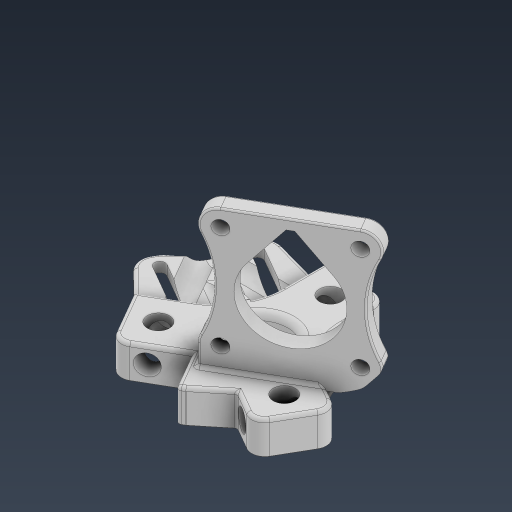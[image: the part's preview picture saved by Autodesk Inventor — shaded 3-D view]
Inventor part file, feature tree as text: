
AUTODESK INVENTOR PART (.ipt)
format: ipt  version: 2024 (Build 280153000, 153)  size: 945,152 bytes
history: native  units: mm
features: sketch x18, extrude x16, fillet x10, chamfer x6, hole x4, projected_geometry x4, plane x3, pattern_circular x2, mirror x1
ambient origin geometry x8: Origin, YZ Plane, XZ Plane, XY Plane, X Axis, Y Axis, Z Axis, Center Point
bodies: Solid1 (feature_tree)
feature tree (64):
  sketch  "Sketch1"  dims[d0=22.0mm d1=12.0mm]
  extrude  "Extrusion1"  Depth=12.0mm
  hole  "Hole1"  [1 undecoded]
  sketch  "Sketch2"  dims[d2=10.0mm d3=0.0mm]
  plane  "Work Plane1"
  plane  "Work Plane2"
  plane  "Work Plane3"
  sketch  "Sketch3"  dims[d4=6.65mm d5=6.0mm d6=4.0mm d7=2.0mm d8=90.0deg d9=8.0mm d10=20.594885mm d11=90.0deg]
  extrude  "Extrusion3"  TaperAngle=90.0deg  [1 undecoded]
  pattern_circular  "Circular Pattern2"  Count=3 Angle=360.0deg
  sketch  "Sketch31"  dims[d85=2.0mm d86=10.0mm d87=12.9mm d88=7.0mm d90=9.15mm d91=10.0mm d92=0.0mm d93=0.0mm d94=0.0mm d113=1.0mm d114=0.0mm d115=5.0mm d116=9.0mm d118=41.0mm d121=42.5mm d122=0.0mm d124=2.0mm d125=6.0mm d126=4.0mm d127=2.0mm d128=90.0deg d129=9.394mm d130=0.0mm d131=3.1mm d132=6.5mm d133=5.0mm d134=2.5mm d153=4.2mm d154=6.0mm d155=8.0mm d156=4.0mm d157=90.0deg d158=9.394mm d159=0.0mm d160=5.0mm d161=31.0mm d162=31.0mm d163=5.0mm d164=30.0mm d166=30.0mm d168=5.0mm d169=0.0mm d173=8.0mm d174=0.0mm d175=0.0mm d176=0.0mm d177=0.0mm d178=8.726646mm d179=10.0mm d180=0.0mm d183=3.4mm d184=2.0mm d185=45.0deg d187=5.0mm d188=2.0mm d189=0.0mm d191=25.0mm d192=8.726646mm d193=8.726646mm d194=0.0mm d195=0.0mm d196=0.5mm d197=1.5mm d198=2.0mm d199=45.0deg d216=4.0mm d217=0.0mm d218=6.601mm d219=25.3mm d220=4.537856mm d221=6.601mm d222=25.3mm d223=4.537856mm d224=5.0mm d225=2.0mm d227=2.0mm d229=1.0mm d230=1.0mm d231=1.0mm d232=4.0mm d233=0.2mm d234=25.3mm d235=4.537856mm d236=0.5mm d237=25.3mm d238=4.537856mm d239=18.0mm d240=0.0mm d241=0.0mm d242=2.0mm d212=0.0mm d213=0.0mm d214=0.0mm d215=0.0mm]
  extrude  "Extrusion21"  Depth=3.0mm TaperAngle=0.0deg
  extrude  "Extrusion4"  TaperAngle=0.0deg  [1 undecoded]
  extrude  "Extrusion5"  Depth=19.365844mm
  pattern_circular  "Circular Pattern4"  [2 undecoded]
  hole  "Hole2"  [1 undecoded]
  mirror  "Mirror1"
  sketch  "Sketch13"  dims[d16=3.325mm]
  extrude  "Extrusion7"  Depth=7.0mm
  extrude  "Extrusion8"  Depth=9.15mm
  extrude  "Extrusion10"  Depth=10.0mm TaperAngle=0.0deg
  hole  "Hole4"  [1 undecoded]
  extrude  "Extrusion11"  Depth=1.0mm TaperAngle=0.0deg
  hole  "Hole5"  [1 undecoded]
  sketch  "Sketch23"  dims[d44=5.1mm d45=0.0mm d46=0.0mm]
  extrude  "Extrusion12"  Depth=42.5mm TaperAngle=0.0deg
  extrude  "Extrusion14"  Depth=3.1mm
  extrude  "Extrusion15"  Depth=6.5mm
  extrude  "Extrusion16"  Depth=5.0mm
  chamfer  "Chamfer1"  Distance=2.5mm
  fillet  "Fillet8"  Radius=5.0mm
  extrude  "Extrusion17"  Depth=31.0mm
  extrude  "Extrusion18"  Depth=31.0mm
  fillet  "Fillet9"  Radius=5.0mm
  chamfer  "Chamfer2"  Distance=30.0mm
  extrude  "Extrusion20"  Depth=30.0mm
  chamfer  "Chamfer6"  Distance=5.0mm
  chamfer  "Chamfer7"  Distance=8.0mm
  fillet  "Fillet15"  [1 undecoded]
  fillet  "Fillet16"  [1 undecoded]
  fillet  "Fillet18"  Radius=8.726646mm
  fillet  "Fillet20"  Radius=10.0mm
  fillet  "Fillet21"  Radius=3.4mm
  fillet  "Fillet22"  Radius=5.0mm
  fillet  "Fillet23"  Radius=2.0mm
  chamfer  "Chamfer8"  Distance=25.0mm
  chamfer  "Chamfer9"  Distance=8.726646mm
  fillet  "Fillet24"  Radius=8.726646mm
  sketch  "Sketch4"  dims[d12=90.0deg d13=90.0deg]
  sketch  "Sketch6"  dims[d14=6.2mm]
  sketch  "Sketch9"  dims[d15=5.0mm]
  sketch  "Sketch18"  dims[d17=6.65mm]
  projected_geometry  "Projected Loop3"
  sketch  "Sketch19"  dims[d23=6.0mm]
  sketch  "Sketch20"  dims[d25=10.0mm d26=0.0mm d27=30.0mm d28=360.0deg]
  sketch  "Sketch22"  dims[d30=17.0mm d31=28.0mm d32=30.94mm d33=4.372mm d34=18.4mm d35=4.662mm d36=4.662mm d37=3.23mm d38=3.23mm d39=6.5mm d40=6.5mm d42=3.0mm d43=0.0mm]
  projected_geometry  "Projected Loop4"
  sketch  "Sketch24"  dims[d50=30.0mm d51=360.0deg]
  sketch  "Sketch25"  dims[d55=8.0mm d56=6.0mm d57=4.0mm d58=2.0mm d59=90.0deg d60=8.0mm d61=20.594885mm d62=19.365844mm]
  sketch  "Sketch26"  dims[d63=19.365844mm]
  sketch  "Sketch27"  dims[d83=90.0deg]
  projected_geometry  "Projected Loop5"
  projected_geometry  "Projected Loop6"
  sketch  "Sketch30"  dims[d84=2.0mm]
note: 10 required parameter values undecoded (feature->parameter linkage not recoverable at this tier; creation-order binding heuristic only, values carry confidence <= 0.55)
